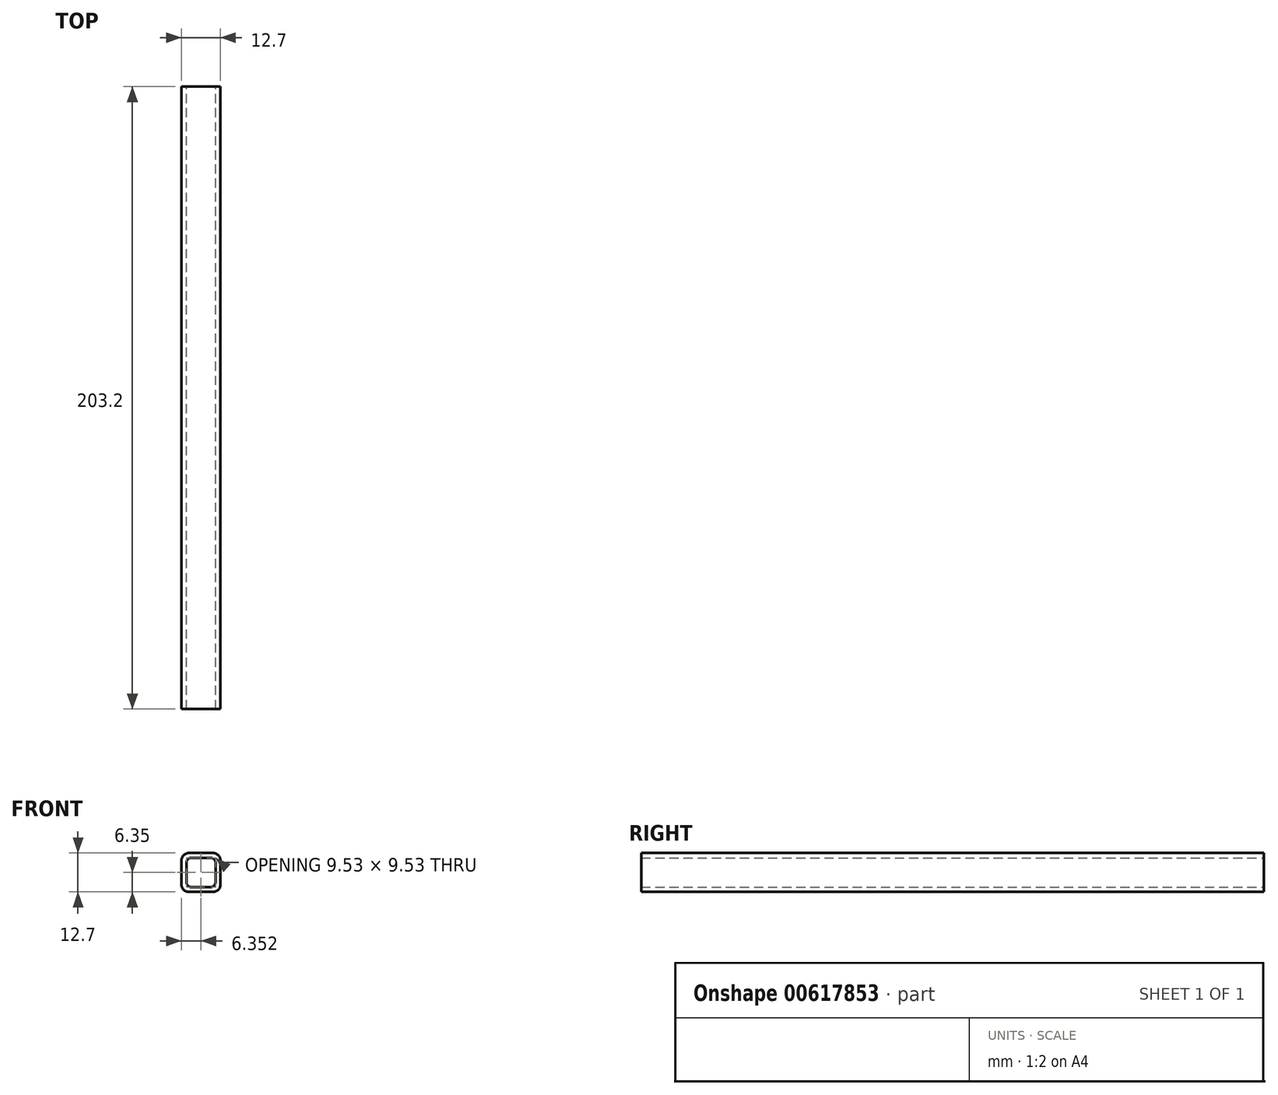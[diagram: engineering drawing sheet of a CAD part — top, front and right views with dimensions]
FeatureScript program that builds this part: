
annotation { "Feature Type Name" : "Feature", "Feature Type Description" : "" }
export const myFeature = defineFeature(function(context is Context, id is Id, definition is map)
    precondition{}
    {
        {
            var Q0;
            Q0=qCreatedBy(makeId("Front.planeOp"),FACE);
            var sketch = newSketch(context, id + "F0", { "sketchPlane" : qUnion([Q0])});
            skLineSegment(sketch, "E0.bottom", {"start": v(7.7, 0) * mm, "end": v(-0.25, 0) * mm});
            skLineSegment(sketch, "E0.top", {"start": v(7.7, -12.7) * mm, "end": v(-0.25, -12.7) * mm});
            skLineSegment(sketch, "E0.left", {"start": v(10.07, -2.38) * mm, "end": v(10.07, -10.32) * mm});
            skLineSegment(sketch, "E0.right", {"start": v(-2.63, -2.38) * mm, "end": v(-2.63, -10.32) * mm});
            skPoint(sketch, "E0.middle", {"position": v(3.72, -6.35) * mm});
            skPoint(sketch, "E1.visualSharp", {"position": v(-2.63, 0) * mm});
            skArc(sketch, "E1.filletArc", {"start": v(-0.25, 0) * mm, "mid": v(-1.93, -0.7) * mm, "end": v(-2.63, -2.38) * mm});
            skPoint(sketch, "E2.visualSharp", {"position": v(-2.63, -12.7) * mm});
            skArc(sketch, "E2.filletArc", {"start": v(-2.63, -10.32) * mm, "mid": v(-1.93, -12) * mm, "end": v(-0.25, -12.7) * mm});
            skPoint(sketch, "E3.visualSharp", {"position": v(10.07, -12.7) * mm});
            skArc(sketch, "E3.filletArc", {"start": v(7.7, -12.7) * mm, "mid": v(9.37, -12) * mm, "end": v(10.07, -10.32) * mm});
            skPoint(sketch, "E4.visualSharp", {"position": v(10.07, 0) * mm});
            skArc(sketch, "E4.filletArc", {"start": v(10.07, -2.38) * mm, "mid": v(9.37, -0.7) * mm, "end": v(7.7, 0) * mm});
            skLineSegment(sketch, "E5.bottom", {"start": v(6.9, -1.59) * mm, "end": v(0.55, -1.59) * mm});
            skLineSegment(sketch, "E5.top", {"start": v(6.9, -11.11) * mm, "end": v(0.55, -11.11) * mm});
            skLineSegment(sketch, "E5.left", {"start": v(8.48, -3.17) * mm, "end": v(8.48, -9.53) * mm});
            skLineSegment(sketch, "E5.right", {"start": v(-1.04, -3.18) * mm, "end": v(-1.04, -9.53) * mm});
            skPoint(sketch, "E6.visualSharp", {"position": v(-1.04, -1.59) * mm});
            skArc(sketch, "E6.filletArc", {"start": v(0.55, -1.59) * mm, "mid": v(-0.58, -2.05) * mm, "end": v(-1.04, -3.18) * mm});
            skPoint(sketch, "E7.visualSharp", {"position": v(8.48, -1.59) * mm});
            skArc(sketch, "E7.filletArc", {"start": v(8.48, -3.17) * mm, "mid": v(8.02, -2.05) * mm, "end": v(6.9, -1.59) * mm});
            skPoint(sketch, "E8.visualSharp", {"position": v(8.48, -11.11) * mm});
            skArc(sketch, "E8.filletArc", {"start": v(6.9, -11.11) * mm, "mid": v(8.02, -10.65) * mm, "end": v(8.48, -9.53) * mm});
            skPoint(sketch, "E9.visualSharp", {"position": v(-1.04, -11.11) * mm});
            skArc(sketch, "E9.filletArc", {"start": v(-1.04, -9.53) * mm, "mid": v(-0.58, -10.65) * mm, "end": v(0.55, -11.11) * mm});
            skSolve(sketch);
        }
        {
            var Q0;
            Q0 = qSketchRegion(id + "F0", true);
            extrude(context, id + "F1", {"entities" : qUnion([Q0]), "depth" : 203.2 * mm, "offsetDistance" : 25.4 * mm});
        }
    });
